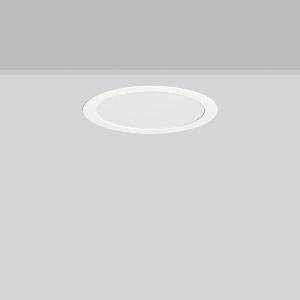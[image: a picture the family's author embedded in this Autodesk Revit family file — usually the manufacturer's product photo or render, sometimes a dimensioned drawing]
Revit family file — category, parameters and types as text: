
# Revit family: toledo_flat__round_e_901808_002_2_730_744c
name_source: partatom
category: Lighting Fixtures
units: mm (PartAtom-declared; Revit-internal decimal feet)

## family parameters
Cut with Voids When Loaded = No
Host = Face
Light Source = No
Part Type = Normal
Room Calculation Point = No
Round Connector Dimension = Use Diameter
Shared = No

## types (1)
- TuneableWhite 827 (1 x LED Modul 827, 2200 lm, 2700)
    Apparent Load = 18 VA
    CIE Flux Codes = 47 79 96 100 100
    Color Rendering = 80
    Color Temperature = 2700
    Default Elevation = 1800 mm
    Description = Series: TOLEDO FLAT+ round
Flexible round recessed multifunction downlight. Housing: sheet steel, powder-coated. Luminaire frame: aluminium, powder-coated. Light guide and diffuser made of non-yellowing PMMA, opal matt. LED backlight technology for homogeneous illumination of the entire light-emitting surface. Tunable white dynamically adjustable from 2700 K to 6500 K. Suitable for Recessed ceiling mounting. Ceiling installation with spring system. Can be directly covered with thermal insulation material (applies only to the lower lumen levels). Including separate LED converter with connecting cable 250 mm. With Casambi smart+free Bluetooth control for wireless network and operation using Android / iOS devices, free app available for download. Surface mounted housing as accessory for all sizes. 
Colour: white
Diameter: 270 mm
Height: 2 mm
Cut-out diameter: 257 mm
Recess height: 60 mm
Luminaire: recess height: 40 mm
Lamp: LED
Socket: without socket
Colour temperature: 2700K - 6500K
Colour rendering index (CRI): 80
System power: 18 W
Rated luminous flux: 2200 lm
Luminous efficiency: 122 lm/W
System power 2: 18 W
Rated luminous flux 2: 2300 lm
Luminous efficiency 2: 128 lm/W
System power 3: 18 W
Rated luminous flux 3: 2300 lm
Luminous efficiency 3: 128 lm/W
Control gear: Dimmable Bluetooth converter
Protection class: II
Type of protection: IP 54
    Height = 0 mm  [stored 0 ft]
    Lamp = 1 x LED Modul 827
    Lamp Light Flux = 2200 lm
    Lamp count = 1
    Length = 270 mm
    Lifetime = 50000 h
    Luminous efficacy = 122 lm/W
    Manufacturer = RZB
    ModVariant = No
    Model = 901808.002.2.730
    Mounting Place = Ceiling
    Mounting Type = Recessed
    Number of Poles = 1
    OnlyDefault = Yes
    Power Factor = 1
    Product Name = TOLEDO FLAT+ round E
    Product group = Recessed downlights
    ProductGroupID = 402
    Protection Class = Protection class II
    Protection Degree = Degree of protection
    RLX_Detail_Level = 1
    RLX_Emergency_Light_Flux = 0 lm
    RLX_Emergency_Type = 0
    RLX_Emergency_Type_DB = No
    RlxData = <blob elided: 30997 chars, md5=67730fa8>
    Socket = socket
    Standby Power = 0 W
    System Light Flux = 2200 lm
    System Power = 18 W
    Type Comments = TuneableWhite 827
    Type Image = 901808.002.jpg
    URL = http://relux.com
    VarID = tuneablewhite_827
    Voltage = 0 V
    Weight = 0.00 kg
    Width = 0 mm  [stored 0 ft]

note: [stored X ft] marks values corroborated as IEEE doubles in the binary element streams (Revit-internal decimal feet)

## geometry (parser evidence)
native form markers: Blend x4, Sweep x10
no freeform markers — native parametric forms only
